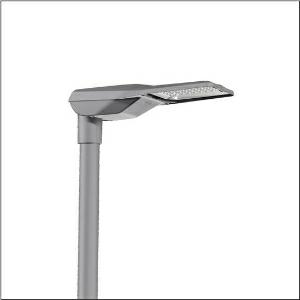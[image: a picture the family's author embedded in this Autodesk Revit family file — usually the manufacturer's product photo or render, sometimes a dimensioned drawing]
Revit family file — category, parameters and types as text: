
# Revit family: streetlight_sl_21_iq_mini___st0_8a_5xe2c21d08hb_7297
name_source: partatom
category: Lighting Fixtures
units: mm (PartAtom-declared; Revit-internal decimal feet)

## family parameters
Cut with Voids When Loaded = No
Host = Face
Light Source = No
Part Type = Normal
Room Calculation Point = No
Round Connector Dimension = Use Diameter
Shared = No

## types (1)
- --- (1 x LED, 7830 lm, 70.9 W, 2200K)
    Apparent Load = 71 VA
    CIE Flux Codes = 38 75 97 100 100
    Color Rendering = 70
    Color Temperature = 2200K
    Default Elevation = 1800 mm
    Description = Streetlight SL 21 iQ mini, mast luminaire, primary light control with lens, of PMMA, primary optical cover: cover, of toughened safety glass, transparent, light distribution: ST0.8a, light emission: direct distribution, primary light characteristic: asymmetric, installation type: post-top, side-entry, LED, High Power LED, rated luminous flux: 7.830lm, luminous efficacy: 110lm/W, light colour: 722, colour temperature: 2200K, control gear: iQ-Comfort, control: Auto-Match, Temp-Guard, Lumen-Switch, Night-Set, Smart-Wire, Light-Fading, Desk-Remote (wireless, voltage-free reading and setting of iQ features in the workshop via application-optimized NFC function/RFID function), optimised constant luminous flux control (CLO 2.0), pre-setting: linear dimming characteristic, mains connection: 220..240V, AC, 50/60Hz, start of lifetime: 71W, end of service life: 75W, reduction: 31W, luminaire housing, of diecast aluminium, powder-coated, SITECO metallic grey (DB 702S), corrosivity category C5 high according to DIN EN ISO 12944, please order mast flange separately, inclination adjustable: 0°, 5°, 10°, 15°, sealing non-destructively replaceable, multi-level sealing system, length: 628mm, width: 235mm, height: 110mm, mast flange for spigot size: 42mm (side-entry): 5XC10008XM4, 60/48mm (side-entry/post-top): 5XC10108XM2, 76/60mm (side-entry/post-top): 5XC10108XM1, mounting height: 4..8m, protection rating (complete): IP66, insulation class (complete): insulation class II (safety insulation), certification: CE, ENEC, ENEC+, VDE, impact resistance: IK10, permissible operating ambient temperature for outdoor applications: -40..+50°C, standard-compliant lighting for roads and squares, packaging unit: 1 piece

Light Distribution: ST0.8a
    Height = 110 mm
    Lamp = 1 x LED
    Lamp Light Flux = 7830 lm
    Lamp Power = 70.9 W
    Lamp count = 1
    Length = 625 mm
    Luminous efficacy = 110 lm/W
    Manufacturer = Siteco
    ModVariant = No
    Model = 5XE2C21D08HB
    Number of Poles = 1
    OnlyDefault = Yes
    Power Factor = 1
    Product Name = Streetlight SL 21 iQ mini | ST0.8a
    Product group = mast luminaire | pylon top
    ProductGroupID = 6100
    Protection Class = Protection class II
    Protection Degree = IP 66
    RLX_Detail_Level = 1
    RLX_Emergency_Light_Flux = 0 lm
    RLX_Emergency_Type = 0
    RLX_Emergency_Type_DB = No
    RlxData = <blob elided: 26257 chars, md5=bee9ca41>
    Socket = socket
    Standby Power = 0 W
    System Light Flux = 7830 lm
    System Power = 71 W
    Type Comments = factory setting: luminous flux: 100 % | dim-lin: 254 | 711 mA
    Type Image = l_1003519.jpg
    URL = http://relux.com
    VarID = @adj_157033
    Voltage = 0 V
    Weight = 0.00 kg
    Width = 234 mm

## geometry (parser evidence)
native form markers: Blend x4, Sweep x11
no freeform markers — native parametric forms only
